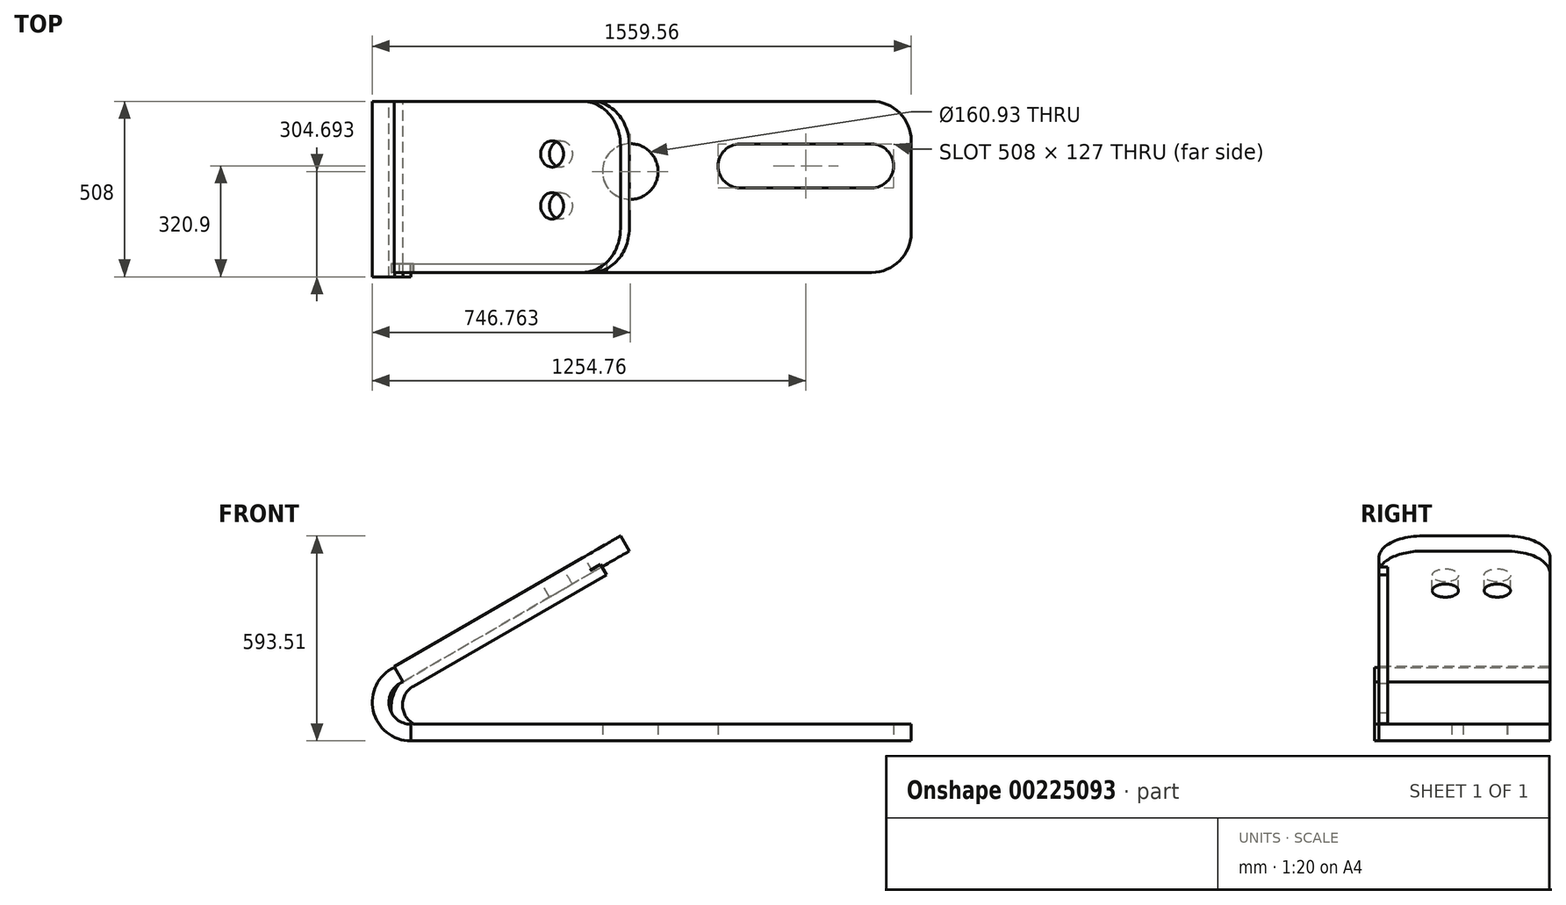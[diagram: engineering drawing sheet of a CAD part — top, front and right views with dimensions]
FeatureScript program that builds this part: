
annotation { "Feature Type Name" : "Feature", "Feature Type Description" : "" }
export const myFeature = defineFeature(function(context is Context, id is Id, definition is map)
    precondition{}
    {
        {
            var Q0;
            Q0=qCreatedBy(makeId("Top.planeOp"),FACE);
            var sketch = newSketch(context, id + "F0", { "sketchPlane" : qUnion([Q0])});
            skLineSegment(sketch, "E0", {"start": v(1010.22, 0) * mm, "end": v(1010.22, 0) * mm});
            skLineSegment(sketch, "E1", {"start": v(1010.22, 0) * mm, "end": v(1010.22, 495.3) * mm});
            skLineSegment(sketch, "E2", {"start": v(1010.22, 495.3) * mm, "end": v(2343.72, 495.3) * mm});
            skLineSegment(sketch, "E3", {"start": v(2458.02, 381) * mm, "end": v(2458.02, 114.3) * mm});
            skLineSegment(sketch, "E4.bottom", {"start": v(1962.72, 371.7) * mm, "end": v(2343.72, 371.7) * mm});
            skLineSegment(sketch, "E4.top", {"start": v(1962.72, 371.7) * mm, "end": v(2343.72, 371.7) * mm});
            skLineSegment(sketch, "E4.left", {"start": v(1962.72, 371.7) * mm, "end": v(1962.72, 371.7) * mm});
            skLineSegment(sketch, "E4.right", {"start": v(2343.72, 371.7) * mm, "end": v(2343.72, 371.7) * mm});
            skLineSegment(sketch, "E5", {"start": v(1962.72, 244.7) * mm, "end": v(2343.72, 244.7) * mm});
            skArc(sketch, "E6", {"start": v(1962.72, 371.7) * mm, "mid": v(1899.22, 308.2) * mm, "end": v(1962.72, 244.7) * mm});
            skArc(sketch, "E7", {"start": v(2343.72, 244.7) * mm, "mid": v(2407.22, 308.2) * mm, "end": v(2343.72, 371.7) * mm});
            skLineSegment(sketch, "E8", {"start": v(1962.72, 244.7) * mm, "end": v(1962.72, 371.7) * mm});
            skLineSegment(sketch, "E9", {"start": v(2343.72, 371.7) * mm, "end": v(2343.72, 244.7) * mm});
            skCircle(sketch, "E10", {"center": v(1645.22, 292) * mm, "radius": 80.47 * mm});
            skLineSegment(sketch, "E11", {"start": v(1010.22, 0) * mm, "end": v(2343.72, 0) * mm});
            skPoint(sketch, "E12.visualSharp", {"position": v(2458.02, 495.3) * mm});
            skArc(sketch, "E12.filletArc", {"start": v(2458.02, 381) * mm, "mid": v(2424.55, 461.82) * mm, "end": v(2343.72, 495.3) * mm});
            skPoint(sketch, "E13.visualSharp", {"position": v(2458.02, 0) * mm});
            skArc(sketch, "E13.filletArc", {"start": v(2343.72, 0) * mm, "mid": v(2424.55, 33.48) * mm, "end": v(2458.02, 114.3) * mm});
            skSolve(sketch);
        }
        {
            var Q0;
            Q0=makeQuery(id+"F0.imprint","IMPRINT",FACE,{"disambiguationData":[TD([[makeQuery(id+"F0.imprint","IMPRINT",EDGE,{"derivedFrom":sQuery(id+"F0.wireOp",EDGE,"E1")}),-1.0]])]});
            extrude(context, id + "F1", {"entities" : qUnion([Q0]), "depth" : 48.26 * mm});
        }
        {
            var Q0;
            Q0=makeQuery(id+"F1.opExtrude","SWEPT_FACE",FACE,{"disambiguationData":[OSD([sQuery(id+"F0.wireOp",EDGE,"E11")])]});
            var sketch = newSketch(context, id + "F2", { "sketchPlane" : qUnion([Q0])});
            skPoint(sketch, "E14", {"position": v(1645.22, 48.26) * mm});
            skLineSegment(sketch, "E15", {"start": v(1010.22, 48.26) * mm, "end": v(1010.22, 48.26) * mm});
            skSolve(sketch);
        }
        {
            var Q0;
            {var subQ0=sQuery(id+"F0.wireOp",EDGE,"E11");Q0=makeQuery(id+"F2.imprint","IMPRINT",FACE,{"disambiguationData":[TD([[makeQuery(id+"F2.imprint","IMPRINT",EDGE,{"derivedFrom":makeQuery(id+"F1.opExtrude","CAP_EDGE",EDGE,{"disambiguationData":[OSD([subQ0])],"isStart":true})}),1.0]])]});}
            var sketch = newSketch(context, id + "F3", { "sketchPlane" : qUnion([Q0])});
            skLineSegment(sketch, "E16", {"start": v(1017.17, 158.46) * mm, "end": v(1576.17, 481.2) * mm});
            skLineSegment(sketch, "E17", {"start": v(1576.17, 481.2) * mm, "end": v(1558.92, 511.07) * mm});
            skLineSegment(sketch, "E18", {"start": v(1558.92, 511.07) * mm, "end": v(1009, 193.57) * mm});
            skLineSegment(sketch, "E19", {"start": v(1009, 193.57) * mm, "end": v(1017.17, 158.46) * mm});
            skArc(sketch, "E20", {"start": v(1009, 193.57) * mm, "mid": v(953.11, 96.79) * mm, "end": v(1009, 0) * mm});
            skArc(sketch, "E21", {"start": v(1017.17, 158.46) * mm, "mid": v(985.96, 104.4) * mm, "end": v(1017.17, 50.35) * mm});
            skLineSegment(sketch, "E22", {"start": v(1009, 0) * mm, "end": v(1017.17, 50.35) * mm});
            skSolve(sketch);
        }
        {
            var Q0;
            Q0 = qSketchRegion(id + "F3", true);
            extrude(context, id + "F4", {"entities" : qUnion([Q0]), "operationType" : NewBodyOperationType.ADD, "oppositeDirection" : true, "depth" : 25.4 * mm});
        }
        {
            var Q0;
            Q0=makeQuery(id+"F1.opExtrude","SWEPT_FACE",FACE,{"disambiguationData":[OSD([sQuery(id+"F0.wireOp",EDGE,"E2")])]});
            var sketch = newSketch(context, id + "F5", { "sketchPlane" : qUnion([Q0])});
            skLineSegment(sketch, "E23", {"start": v(-1536.68, 488.58) * mm, "end": v(-986.75, 171.08) * mm});
            skLineSegment(sketch, "E24", {"start": v(-1536.68, 488.58) * mm, "end": v(-1512.55, 530.38) * mm});
            skLineSegment(sketch, "E25", {"start": v(-1512.55, 530.38) * mm, "end": v(-962.62, 212.88) * mm});
            skLineSegment(sketch, "E26", {"start": v(-962.62, 212.88) * mm, "end": v(-986.75, 171.08) * mm});
            skArc(sketch, "E27", {"start": v(-1010.22, 0) * mm, "mid": v(-901.16, 87.37) * mm, "end": v(-962.62, 212.88) * mm});
            skArc(sketch, "E28", {"start": v(-1010.22, 48.26) * mm, "mid": v(-947.7, 99.97) * mm, "end": v(-986.75, 171.08) * mm});
            skSolve(sketch);
        }
        {
            var Q0;
            Q0=makeQuery(id+"F5.imprint","IMPRINT",FACE,{"disambiguationData":[TD([[makeQuery(id+"F5.imprint","IMPRINT",EDGE,{"derivedFrom":sQuery(id+"F5.wireOp",EDGE,"E26")}),1.0]])]});
            var Q1;
            Q1=makeQuery(id+"F5.imprint","IMPRINT",FACE,{"disambiguationData":[TD([[makeQuery(id+"F5.imprint","IMPRINT",EDGE,{"derivedFrom":sQuery(id+"F5.wireOp",EDGE,"E23")}),1.0]])]});
            extrude(context, id + "F6", {"entities" : qUnion([Q0, Q1]), "oppositeDirection" : true, "depth" : 25.4 * mm});
        }
        {
            var Q0;
            Q0=makeQuery(id+"F6.opExtrude","SWEPT_FACE",FACE,{"disambiguationData":[OSD([sQuery(id+"F5.wireOp",EDGE,"E25")])]});
            var sketch = newSketch(context, id + "F7", { "sketchPlane" : qUnion([Q0])});
            skLineSegment(sketch, "E29", {"start": v(940.1, 495.3) * mm, "end": v(940.1, 0) * mm});
            skLineSegment(sketch, "E30", {"start": v(940.1, 0) * mm, "end": v(1569.97, 0) * mm});
            skLineSegment(sketch, "E31", {"start": v(1696.97, 127) * mm, "end": v(1696.97, 368.3) * mm});
            skLineSegment(sketch, "E32", {"start": v(940.1, 495.3) * mm, "end": v(1569.97, 495.3) * mm});
            skPoint(sketch, "E33.visualSharp", {"position": v(1696.97, 0) * mm});
            skArc(sketch, "E33.filletArc", {"start": v(1569.97, 0) * mm, "mid": v(1659.77, 37.2) * mm, "end": v(1696.97, 127) * mm});
            skPoint(sketch, "E34.visualSharp", {"position": v(1696.97, 495.3) * mm});
            skArc(sketch, "E34.filletArc", {"start": v(1696.97, 368.3) * mm, "mid": v(1659.77, 458.1) * mm, "end": v(1569.97, 495.3) * mm});
            skSolve(sketch);
        }
        {
            var Q0;
            Q0 = qSketchRegion(id + "F7", true);
            extrude(context, id + "F8", {"entities" : qUnion([Q0]), "operationType" : NewBodyOperationType.ADD, "oppositeDirection" : true, "depth" : 48.26 * mm});
        }
        {
            var Q0;
            Q0 = qSketchRegion(id + "F7", true);
            extrude(context, id + "F9", {"entities" : qUnion([Q0]), "operationType" : NewBodyOperationType.ADD, "depth" : 2.54 * mm});
        }
        {
            var Q0;
            Q0=makeQuery(id+"F6.opExtrude","CAP_FACE",FACE,{"disambiguationData":[OSD([sQuery(id+"F0.wireOp",EDGE,"E1"),sQuery(id+"F0.wireOp",EDGE,"E2"),sQuery(id+"F5.wireOp",EDGE,"E23"),sQuery(id+"F5.wireOp",EDGE,"E24"),sQuery(id+"F5.wireOp",EDGE,"E25"),sQuery(id+"F5.wireOp",EDGE,"E27"),sQuery(id+"F5.wireOp",EDGE,"E28")])],"isStart":false});
            var sketch = newSketch(context, id + "F10", { "sketchPlane" : qUnion([Q0])});
            skArc(sketch, "E35", {"start": v(962.62, 212.88) * mm, "mid": v(901.16, 87.37) * mm, "end": v(1010.22, 0) * mm});
            skPoint(sketch, "E35.midSnap0", {"position": v(901.16, 87.37) * mm});
            skPoint(sketch, "E35.midSnap1", {"position": v(947.7, 99.97) * mm});
            skArc(sketch, "E36", {"start": v(986.75, 171.08) * mm, "mid": v(947.7, 99.97) * mm, "end": v(1010.22, 48.26) * mm});
            skLineSegment(sketch, "E37", {"start": v(1010.22, 0) * mm, "end": v(1010.22, 48.26) * mm});
            skLineSegment(sketch, "E38", {"start": v(986.75, 171.08) * mm, "end": v(962.62, 212.88) * mm});
            skSolve(sketch);
        }
        {
            var Q0;
            Q0 = qSketchRegion(id + "F10", true);
            extrude(context, id + "F11", {"entities" : qUnion([Q0]), "operationType" : NewBodyOperationType.ADD, "depth" : 482.6 * mm});
        }
        {
            var Q0;
            Q0=makeQuery(id+"F9.opExtrude","CAP_FACE",FACE,{"disambiguationData":[OSD([sQuery(id+"F7.wireOp",EDGE,"E29"),sQuery(id+"F7.wireOp",EDGE,"E30"),sQuery(id+"F7.wireOp",EDGE,"E31"),sQuery(id+"F7.wireOp",EDGE,"E32"),sQuery(id+"F7.wireOp",EDGE,"E33.filletArc"),sQuery(id+"F7.wireOp",EDGE,"E34.filletArc")])],"isStart":false});
            var sketch = newSketch(context, id + "F12", { "sketchPlane" : qUnion([Q0])});
            skCircle(sketch, "E39", {"center": v(1468.37, 342.9) * mm, "radius": 38.1 * mm});
            skPoint(sketch, "E40", {"position": v(1087.17, 367.17) * mm});
            skPoint(sketch, "E41", {"position": v(1087.17, 152.73) * mm});
            skCircle(sketch, "E42", {"center": v(1468.37, 192.62) * mm, "radius": 38.1 * mm});
            skSolve(sketch);
        }
        {
            var Q0;
            Q0=makeQuery(id+"F12.imprint","IMPRINT",FACE,{"disambiguationData":[TD([[makeQuery(id+"F12.imprint","IMPRINT",EDGE,{"derivedFrom":sQuery(id+"F12.wireOp",EDGE,"E39")}),1.0]])]});
            var Q1;
            Q1=makeQuery(id+"F12.imprint","IMPRINT",FACE,{"disambiguationData":[TD([[makeQuery(id+"F12.imprint","IMPRINT",EDGE,{"derivedFrom":sQuery(id+"F12.wireOp",EDGE,"E42")}),1.0]])]});
            extrude(context, id + "F13", {"entities" : qUnion([Q0, Q1]), "operationType" : NewBodyOperationType.REMOVE, "endBound" : BoundingType.SYMMETRIC, "oppositeDirection" : true, "depth" : 254 * mm});
        }
    });
